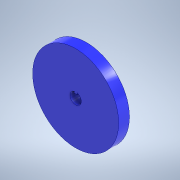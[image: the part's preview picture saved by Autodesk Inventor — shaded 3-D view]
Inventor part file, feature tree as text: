
AUTODESK INVENTOR PART (.ipt)
format: ipt  version: 2021.1 (Build 251245010, 245A)  size: 221,184 bytes
history: native  units: in
note: dims shown in document units (in); Inventor stores cm internally (conversion verified against a paired STEP export)
features: sketch x5, extrude x4, plane x1, hole x1
ambient origin geometry x8: Origin, YZ Plane, XZ Plane, XY Plane, X Axis, Y Axis, Z Axis, Center Point
bodies: Solid1 (feature_tree)
feature tree (11):
  extrude  "Extrusion1"  Depth=0.375in
  extrude  "Extrusion2"  Depth=1.195in
  extrude  "Extrusion3"  TaperAngle=0.0deg  [1 undecoded]
  plane  "Work Plane2"
  hole  "Hole1"  [1 undecoded]
  extrude  "Extrusion4"  TaperAngle=0.0deg  [1 undecoded]
  sketch  "Sketch1"  dims[d0=3.0in d1=0.375in]
  sketch  "Sketch2"  dims[d2=0.0in d3=1.195in]
  sketch  "Sketch3"  dims[d4=0.625in d5=0.0in]
  sketch  "Sketch4"  dims[d6=0.395in d7=0.0938in]
  sketch  "Sketch5"  dims[d8=0.0569in d9=0.0in d10=0.0in d15=0.4in d16=-0.5975in d17=0.201in d18=0.38in d19=0.257in d20=0.31in d21=0.5635in d22=0.45in d23=0.0in d24=2.0in d25=0.1in d26=0.0in]
note: 3 required parameter values undecoded (feature->parameter linkage not recoverable at this tier; creation-order binding heuristic only, values carry confidence <= 0.55)
